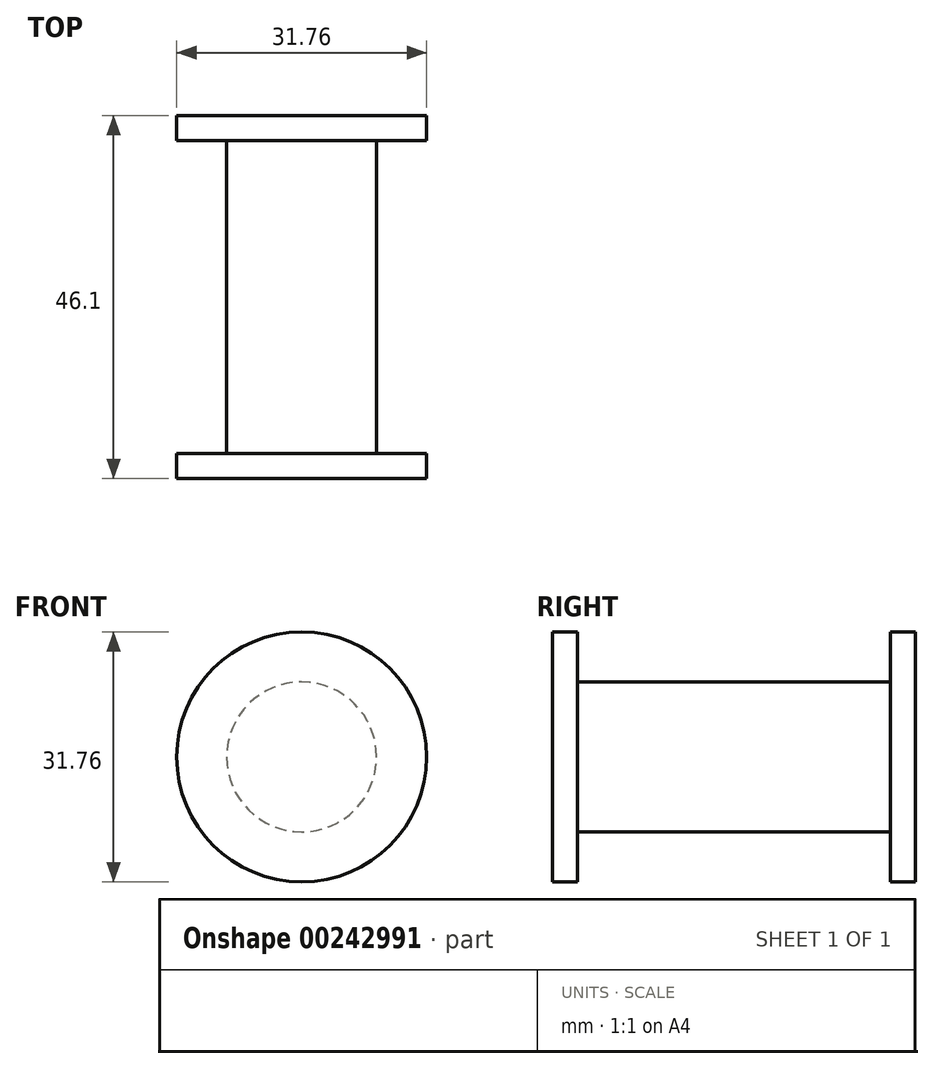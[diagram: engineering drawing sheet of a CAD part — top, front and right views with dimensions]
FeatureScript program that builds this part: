
annotation { "Feature Type Name" : "Feature", "Feature Type Description" : "" }
export const myFeature = defineFeature(function(context is Context, id is Id, definition is map)
    precondition{}
    {
        {
            var Q0;
            Q0=qCreatedBy(makeId("Right.planeOp"),FACE);
            var sketch = newSketch(context, id + "F0", { "sketchPlane" : qUnion([Q0])});
            skLineSegment(sketch, "E0", {"start": v(0, 0) * mm, "end": v(-64.28, 0) * mm, "construction": true});
            skLineSegment(sketch, "E1", {"start": v(0, 0) * mm, "end": v(0, 15.88) * mm});
            skLineSegment(sketch, "E2", {"start": v(0, 15.88) * mm, "end": v(-3.18, 15.88) * mm});
            skLineSegment(sketch, "E3", {"start": v(-3.18, 15.88) * mm, "end": v(-3.18, 9.53) * mm});
            skLineSegment(sketch, "E4", {"start": v(-3.18, 9.53) * mm, "end": v(-42.93, 9.52) * mm});
            skLineSegment(sketch, "E5", {"start": v(-42.93, 9.52) * mm, "end": v(-42.93, 15.87) * mm});
            skLineSegment(sketch, "E6", {"start": v(-42.93, 15.87) * mm, "end": v(-46.1, 15.87) * mm});
            skLineSegment(sketch, "E7", {"start": v(-46.1, 15.87) * mm, "end": v(-46.1, 0) * mm});
            skLineSegment(sketch, "E8", {"start": v(-46.1, 0) * mm, "end": v(0, 0) * mm});
            skSolve(sketch);
        }
        {
            var Q0;
            Q0 = qSketchRegion(id + "F0", true);
            var Q1;
            Q1=sQuery(id+"F0.wireOp",EDGE,"E0");
            revolve(context, id + "F1", {"entities" : qUnion([Q0]), "axis" : qUnion([Q1]), "revolveType" : RevolveType.FULL});
        }
    });
